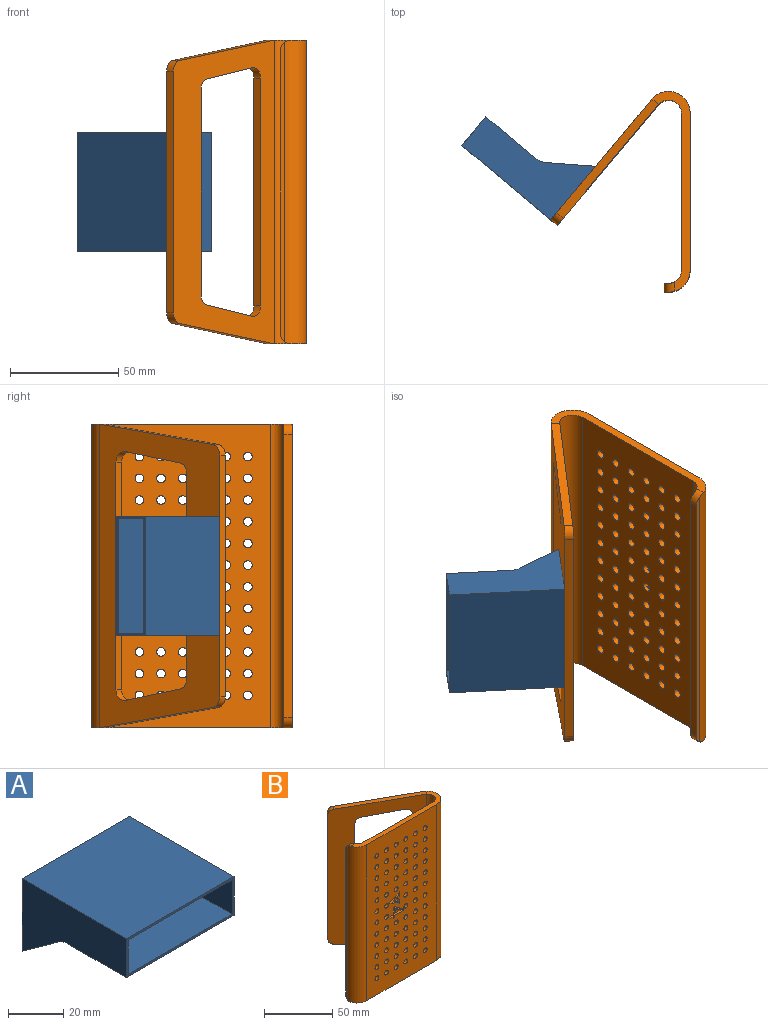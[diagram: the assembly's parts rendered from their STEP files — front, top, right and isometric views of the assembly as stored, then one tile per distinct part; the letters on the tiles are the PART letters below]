
ASSEMBLY  parts=2 mates=1
PART A: 13 faces, bbox 55.2x53.4x32.2 mm
  f0: plane 55.2x53.4mm, normal (0,0,1), area 2947.7mm2, adj f1,f7,f8,f9
  f1: plane 53.4x32.2mm, normal (-1,0,0), area 1075.7mm2, adj f0,f2,f8,f9,f11,f12
  f2: plane 55.2x29.95mm, normal (0,0,-1), area 1653.4mm2, adj f1,f7,f8,f12
  f3: plane 51.9x15.2mm, normal (1,0,0), area 788.9mm2, adj f4,f6,f8,f10
  f4: plane 53.2x51.9mm, normal (0,0,-1), area 2761.1mm2, adj f3,f5,f8,f10
  f5: plane 51.9x15.2mm, normal (-1,0,0), area 788.9mm2, adj f4,f6,f8,f10
  f6: plane 53.2x51.9mm, normal (0,0,1), area 2761.1mm2, adj f3,f5,f8,f10
  f7: plane 53.4x32.2mm, normal (1,0,0), area 1075.7mm2, adj f0,f2,f8,f9,f11,f12
  f8: plane 55.2x17.2mm, normal (0,-1,0), area 140.8mm2, adj f0,f1,f2,f3,f4,f5,f6,f7
  f9: plane 55.2x32.2mm, normal (0,1,0), area 1777.4mm2, adj f0,f1,f7,f11
  f10: plane 53.2x15.2mm, normal (0,-1,0), area 808.6mm2, adj f3,f4,f5,f6
  f11: plane 55.2x18.78mm, normal (0,-0.58,-0.81), area 1276.5mm2, adj f1,f7,f9,f12
  f12: cylinder r=8mm len=55.2mm, axis (-1,0,0), area 275.2mm2, adj f1,f2,f7,f11
PART B: 139 faces, bbox 92.5x64.3x140 mm
  f0: plane 2.47x1.86mm, normal (0,-1,0), area 1.8mm2, adj f1,f4,f89
  f1: plane 2.04x2mm, normal (-0.37,0,-0.93), area 4.4mm2, adj f0,f4,f58,f89
  f2: plane 2x1.78mm, normal (-0.37,0,-0.93), area 3.8mm2, adj f10,f50,f58,f89
  f3: plane 2.69x2mm, normal (-0.39,0,0.92), area 5.8mm2, adj f10,f51,f58,f89
  f4: plane 2.47x2mm, normal (-0.39,0,0.92), area 5.4mm2, adj f0,f1,f58,f89
  f5: plane 2x0.04mm, normal (0,0,-1), area 0.1mm2, adj f8,f9,f43,f88
  f6: plane 3.67x2mm, normal (0,0,-1), area 7.3mm2, adj f41,f43,f44,f88
  f7: plane 2.84x2mm, normal (-1,0,0), area 5.7mm2, adj f40,f43,f44,f88
  f8: plane 2x0.06mm, normal (-1,0,0), area 0.1mm2, adj f5,f9,f43,f88
  f9: plane 0.06x0.04mm, normal (0,-1,0), area 0mm2, adj f5,f8,f88
  f10: plane 140x72.53mm, normal (0,-1,0), area 9168.1mm2, adj f2,f3,f14,f15,f17,f18,f30,f31
  f11: plane 140x55.56mm, normal (0.64,0.77,0), area 4776.3mm2, adj f12,f18,f26,f27,f28,f29,f131,f132
  f12: plane 111.28x3.06mm, normal (-0.77,0.64,0), area 445.1mm2, adj f11,f13,f28,f29
  f13: plane 140x55.56mm, normal (-0.64,-0.77,0), area 4776.3mm2, adj f12,f19,f26,f27,f28,f29,f131,f132
  f14: plane 92.06x17.66mm, normal (0,0,1), area 406.2mm2, adj f10,f17,f18,f19,f20,f21,f25,f27
  f15: plane 92.06x17.66mm, normal (0,0,-1), area 406.2mm2, adj f10,f17,f18,f19,f20,f21,f24,f26
  f16: plane 138x2mm, normal (-1,0,0), area 271.2mm2, adj f17,f23,f24,f25
  f17: cylinder r=10mm len=140mm, axis (0,0,-1), area 2197.2mm2, adj f10,f14,f15,f16,f24,f25
  f18: cylinder r=10mm len=140mm, axis (0,0,-1), area 3420.8mm2, adj f10,f11,f14,f15
  f19: cylinder r=6mm len=140mm, axis (0,0,-1), area 2052.5mm2, adj f13,f14,f15,f20
  f20: plane 140x72.53mm, normal (0,1,0), area 9248.8mm2, adj f14,f15,f19,f21,f59,f60,f61,f62
  f21: cylinder r=6mm len=140mm, axis (0,0,-1), area 1317.5mm2, adj f14,f15,f20,f22,f24,f25
  f22: plane 138x2mm, normal (1,0,0), area 271.2mm2, adj f21,f23,f24,f25
  f23: plane 130x4mm, normal (0,1,0), area 520mm2, adj f16,f22,f24,f25
  f24: cylinder r=5mm len=5mm, axis (-1,0,0), area 31.7mm2, adj f15,f16,f17,f21,f22,f23
  f25: cylinder r=5mm len=5mm, axis (1,0,0), area 31.7mm2, adj f14,f16,f17,f21,f22,f23
  f26: plane 54.82x46.91mm, normal (-0.1,0.09,-0.99), area 275.4mm2, adj f11,f13,f15,f29
  f27: plane 54.82x46.91mm, normal (-0.1,0.09,0.99), area 275.4mm2, adj f11,f13,f14,f28
  f28: cylinder r=5mm len=5.88mm, axis (0.64,0.77,0), area 28.7mm2, adj f11,f12,f13,f27
  f29: cylinder r=5mm len=5.88mm, axis (-0.64,-0.77,0), area 28.7mm2, adj f11,f12,f13,f26
  f30: plane 2x1.89mm, normal (1,0,0), area 3.8mm2, adj f10,f31,f42,f43
  f31: plane 2x1.49mm, normal (0,0,1), area 3mm2, adj f10,f30,f32,f43
  f32: plane 2x1.89mm, normal (-1,0,0), area 3.8mm2, adj f10,f31,f33,f43
  f33: plane 9.45x2mm, normal (0,0,1), area 18.9mm2, adj f10,f32,f34,f43
  f34: plane 2x1.19mm, normal (-1,0,0), area 2.4mm2, adj f10,f33,f35,f43
  f35: plane 9.56x6.8mm, normal (-0.58,0,-0.81), area 23.5mm2, adj f10,f34,f36,f43
  f36: plane 2x1.38mm, normal (0,0,-1), area 2.8mm2, adj f10,f35,f37,f43
  f37: plane 6.21x2mm, normal (1,0,0), area 12.4mm2, adj f10,f36,f38,f43
  f38: plane 3.06x2mm, normal (0,0,-1), area 6.1mm2, adj f10,f37,f39,f43
  f39: plane 2x1.79mm, normal (1,0,0), area 3.6mm2, adj f10,f38,f42,f43
  f40: plane 7.01x4.99mm, normal (0.58,0,0.81), area 17.2mm2, adj f7,f41,f43,f44
  f41: plane 2x0.05mm, normal (1,0,0), area 0.1mm2, adj f6,f40,f43,f44
  f42: plane 3.06x2mm, normal (0,0,1), area 6.1mm2, adj f10,f30,f39,f43
  f43: plane 14x9.89mm, normal (0,-1,0), area 42.9mm2, adj f5,f6,f7,f8,f30,f31,f32,f33
  f44: plane 7.01x5.04mm, normal (0,-1,0), area 7.8mm2, adj f6,f7,f40,f41,f88
  f45: plane 9.29x3.92mm, normal (0.39,0,0.92), area 20.2mm2, adj f10,f46,f57,f58
  f46: plane 2x0.93mm, normal (0.97,0,0.23), area 1.9mm2, adj f10,f45,f47,f58
  f47: plane 2x0.47mm, normal (0,0,1), area 0.9mm2, adj f10,f46,f48,f58
  f48: plane 3.61x2mm, normal (-1,0,0), area 7.2mm2, adj f10,f47,f49,f58
  f49: plane 2x0.47mm, normal (0,0,-1), area 0.9mm2, adj f10,f48,f50,f58
  f50: plane 2x1.55mm, normal (0.99,0,-0.17), area 3.1mm2, adj f2,f10,f49,f58
  f51: plane 2x1.55mm, normal (0.98,0,0.18), area 3.1mm2, adj f3,f10,f52,f58
  f52: plane 2x0.47mm, normal (0,0,1), area 0.9mm2, adj f10,f51,f53,f58
  f53: plane 4.55x2mm, normal (-1,0,0), area 9.1mm2, adj f10,f52,f54,f58
  f54: plane 2x0.47mm, normal (0,0,-1), area 0.9mm2, adj f10,f53,f55,f58
  f55: plane 2x1mm, normal (0.97,0,-0.25), area 2.1mm2, adj f10,f54,f56,f58
  f56: plane 9.25x4.02mm, normal (0.4,0,-0.92), area 20.2mm2, adj f10,f55,f57,f58
  f57: plane 2x0.77mm, normal (1,0,0), area 1.5mm2, adj f10,f45,f56,f58
  f58: plane 10.64x9.97mm, normal (0,-1,0), area 28.2mm2, adj f1,f2,f3,f4,f45,f46,f47,f48
  f59: cylinder r=2mm len=4mm, axis (0,1,0), area 50.3mm2, adj f10,f20
  f60: cylinder r=2mm len=4mm, axis (0,1,0), area 50.3mm2, adj f10,f20
  f61: cylinder r=2mm len=4mm, axis (0,1,0), area 50.3mm2, adj f10,f20
  f62: cylinder r=2mm len=4mm, axis (0,1,0), area 50.3mm2, adj f10,f20
  f63: cylinder r=2mm len=4mm, axis (0,1,0), area 50.3mm2, adj f10,f20
  f64: cylinder r=2mm len=4mm, axis (0,1,0), area 50.3mm2, adj f10,f20
  f65: cylinder r=2mm len=4mm, axis (0,1,0), area 50.3mm2, adj f10,f20
  f66: cylinder r=2mm len=4mm, axis (0,1,0), area 50.3mm2, adj f10,f20
  f67: cylinder r=2mm len=4mm, axis (0,1,0), area 50.3mm2, adj f10,f20
  f68: cylinder r=2mm len=4mm, axis (0,1,0), area 50.3mm2, adj f10,f20
  f69: cylinder r=2mm len=4mm, axis (0,1,0), area 50.3mm2, adj f10,f20
  f70: cylinder r=2mm len=4mm, axis (0,1,0), area 50.3mm2, adj f10,f20
  f71: cylinder r=2mm len=4mm, axis (0,1,0), area 50.3mm2, adj f10,f20
  f72: cylinder r=2mm len=4mm, axis (0,1,0), area 50.3mm2, adj f10,f20
  f73: cylinder r=2mm len=4mm, axis (0,1,0), area 50.3mm2, adj f10,f20
  f74: cylinder r=2mm len=4mm, axis (0,1,0), area 50.3mm2, adj f10,f20
  f75: cylinder r=2mm len=4mm, axis (0,1,0), area 50.3mm2, adj f10,f20
  f76: cylinder r=2mm len=4mm, axis (0,1,0), area 50.3mm2, adj f10,f20
  f77: cylinder r=2mm len=4mm, axis (0,1,0), area 50.3mm2, adj f10,f20
  f78: cylinder r=2mm len=4mm, axis (0,1,0), area 50.3mm2, adj f10,f20
  f79: cylinder r=2mm len=4mm, axis (0,1,0), area 50.3mm2, adj f10,f20
  f80: cylinder r=2mm len=4mm, axis (0,1,0), area 50.3mm2, adj f10,f20
  f81: cylinder r=2mm len=4mm, axis (0,1,0), area 50.3mm2, adj f10,f20
  f82: cylinder r=2mm len=4mm, axis (0,1,0), area 50.3mm2, adj f10,f20
  f83: cylinder r=2mm len=4mm, axis (0,1,0), area 50.3mm2, adj f10,f20
  f84: cylinder r=2mm len=4mm, axis (0,1,0), area 50.3mm2, adj f10,f20
  f85: cylinder r=2mm len=4mm, axis (0,1,0), area 50.3mm2, adj f10,f20
  f86: cylinder r=2mm len=4mm, axis (0,1,0), area 50.3mm2, adj f10,f20
  f87: cylinder r=2mm len=4mm, axis (0,1,0), area 50.3mm2, adj f10,f20
  f88: cylinder r=2mm len=4mm, axis (0,1,0), area 38mm2, adj f5,f6,f7,f8,f9,f20,f43,f44
  f89: cylinder r=2mm len=4mm, axis (0,1,0), area 39.4mm2, adj f0,f1,f2,f3,f4,f10,f20,f58
  f90: cylinder r=2mm len=4mm, axis (0,1,0), area 50.3mm2, adj f10,f20
  f91: cylinder r=2mm len=4mm, axis (0,1,0), area 50.3mm2, adj f10,f20
  f92: cylinder r=2mm len=4mm, axis (0,1,0), area 50.3mm2, adj f10,f20
  f93: cylinder r=2mm len=4mm, axis (0,1,0), area 50.3mm2, adj f10,f20
  f94: cylinder r=2mm len=4mm, axis (0,1,0), area 50.3mm2, adj f10,f20
  f95: cylinder r=2mm len=4mm, axis (0,1,0), area 50.3mm2, adj f10,f20
  f96: cylinder r=2mm len=4mm, axis (0,1,0), area 50.3mm2, adj f10,f20
  f97: cylinder r=2mm len=4mm, axis (0,1,0), area 50.3mm2, adj f10,f20
  f98: cylinder r=2mm len=4mm, axis (0,1,0), area 50.3mm2, adj f10,f20
  f99: cylinder r=2mm len=4mm, axis (0,1,0), area 50.3mm2, adj f10,f20
  f100: cylinder r=2mm len=4mm, axis (0,1,0), area 50.3mm2, adj f10,f20
  f101: cylinder r=2mm len=4mm, axis (0,1,0), area 50.3mm2, adj f10,f20
  f102: cylinder r=2mm len=4mm, axis (0,1,0), area 50.3mm2, adj f10,f20
  f103: cylinder r=2mm len=4mm, axis (0,1,0), area 50.3mm2, adj f10,f20
  f104: cylinder r=2mm len=4mm, axis (0,1,0), area 50.3mm2, adj f10,f20
  f105: cylinder r=2mm len=4mm, axis (0,1,0), area 50.3mm2, adj f10,f20
  f106: cylinder r=2mm len=4mm, axis (0,1,0), area 50.3mm2, adj f10,f20
  f107: cylinder r=2mm len=4mm, axis (0,1,0), area 50.3mm2, adj f10,f20
  f108: cylinder r=2mm len=4mm, axis (0,1,0), area 50.3mm2, adj f10,f20
  f109: cylinder r=2mm len=4mm, axis (0,1,0), area 50.3mm2, adj f10,f20
  f110: cylinder r=2mm len=4mm, axis (0,1,0), area 50.3mm2, adj f10,f20
  f111: cylinder r=2mm len=4mm, axis (0,1,0), area 50.3mm2, adj f10,f20
  f112: cylinder r=2mm len=4mm, axis (0,1,0), area 50.3mm2, adj f10,f20
  f113: cylinder r=2mm len=4mm, axis (0,1,0), area 50.3mm2, adj f10,f20
  f114: cylinder r=2mm len=4mm, axis (0,1,0), area 50.3mm2, adj f10,f20
  f115: cylinder r=2mm len=4mm, axis (0,1,0), area 50.3mm2, adj f10,f20
  f116: cylinder r=2mm len=4mm, axis (0,1,0), area 50.3mm2, adj f10,f20
  f117: cylinder r=2mm len=4mm, axis (0,1,0), area 50.3mm2, adj f10,f20
  f118: cylinder r=2mm len=4mm, axis (0,1,0), area 50.3mm2, adj f10,f20
  f119: cylinder r=2mm len=4mm, axis (0,1,0), area 50.3mm2, adj f10,f20
  f120: cylinder r=2mm len=4mm, axis (0,1,0), area 50.3mm2, adj f10,f20
  f121: cylinder r=2mm len=4mm, axis (0,1,0), area 50.3mm2, adj f10,f20
  f122: cylinder r=2mm len=4mm, axis (0,1,0), area 50.3mm2, adj f10,f20
  f123: cylinder r=2mm len=4mm, axis (0,1,0), area 50.3mm2, adj f10,f20
  f124: cylinder r=2mm len=4mm, axis (0,1,0), area 50.3mm2, adj f10,f20
  f125: cylinder r=2mm len=4mm, axis (0,1,0), area 50.3mm2, adj f10,f20
  f126: cylinder r=2mm len=4mm, axis (0,1,0), area 50.3mm2, adj f10,f20
  f127: cylinder r=2mm len=4mm, axis (0,1,0), area 50.3mm2, adj f10,f20
  f128: cylinder r=2mm len=4mm, axis (0,1,0), area 50.3mm2, adj f10,f20
  f129: cylinder r=2mm len=4mm, axis (0,1,0), area 50.3mm2, adj f10,f20
  f130: cylinder r=2mm len=4mm, axis (0,1,0), area 50.3mm2, adj f10,f20
  f131: plane 94.42x3.06mm, normal (0.77,-0.64,0), area 377.7mm2, adj f11,f13,f135,f136
  f132: plane 27.49x23.97mm, normal (0.12,-0.1,0.99), area 131.8mm2, adj f11,f13,f135,f137
  f133: plane 27.49x23.97mm, normal (0.12,-0.1,-0.99), area 131.8mm2, adj f11,f13,f136,f138
  f134: plane 104.82x3.06mm, normal (-0.77,0.64,0), area 419.3mm2, adj f11,f13,f137,f138
  f135: cylinder r=5mm len=5.8mm, axis (-0.64,-0.77,0), area 28.2mm2, adj f11,f13,f131,f132
  f136: cylinder r=5mm len=5.8mm, axis (-0.64,-0.77,0), area 28.2mm2, adj f11,f13,f131,f133
  f137: cylinder r=5mm len=7.01mm, axis (-0.64,-0.77,0), area 34.6mm2, adj f11,f13,f132,f134
  f138: cylinder r=5mm len=7.01mm, axis (-0.64,-0.77,0), area 34.6mm2, adj f11,f13,f133,f134
PLACE A rot(axis=(0.67,0.31,-0.67),145.2deg) t=(-32.16,18.62,23.75)mm
PLACE B rot(axis=(0,0,1),90deg) t=(-20.21,31.31,-52.86)mm
MATE fastened A.f9 <-> B.f11  axis (0.77,-0.64,0) through (-38.45,11.12,17.14)mm
